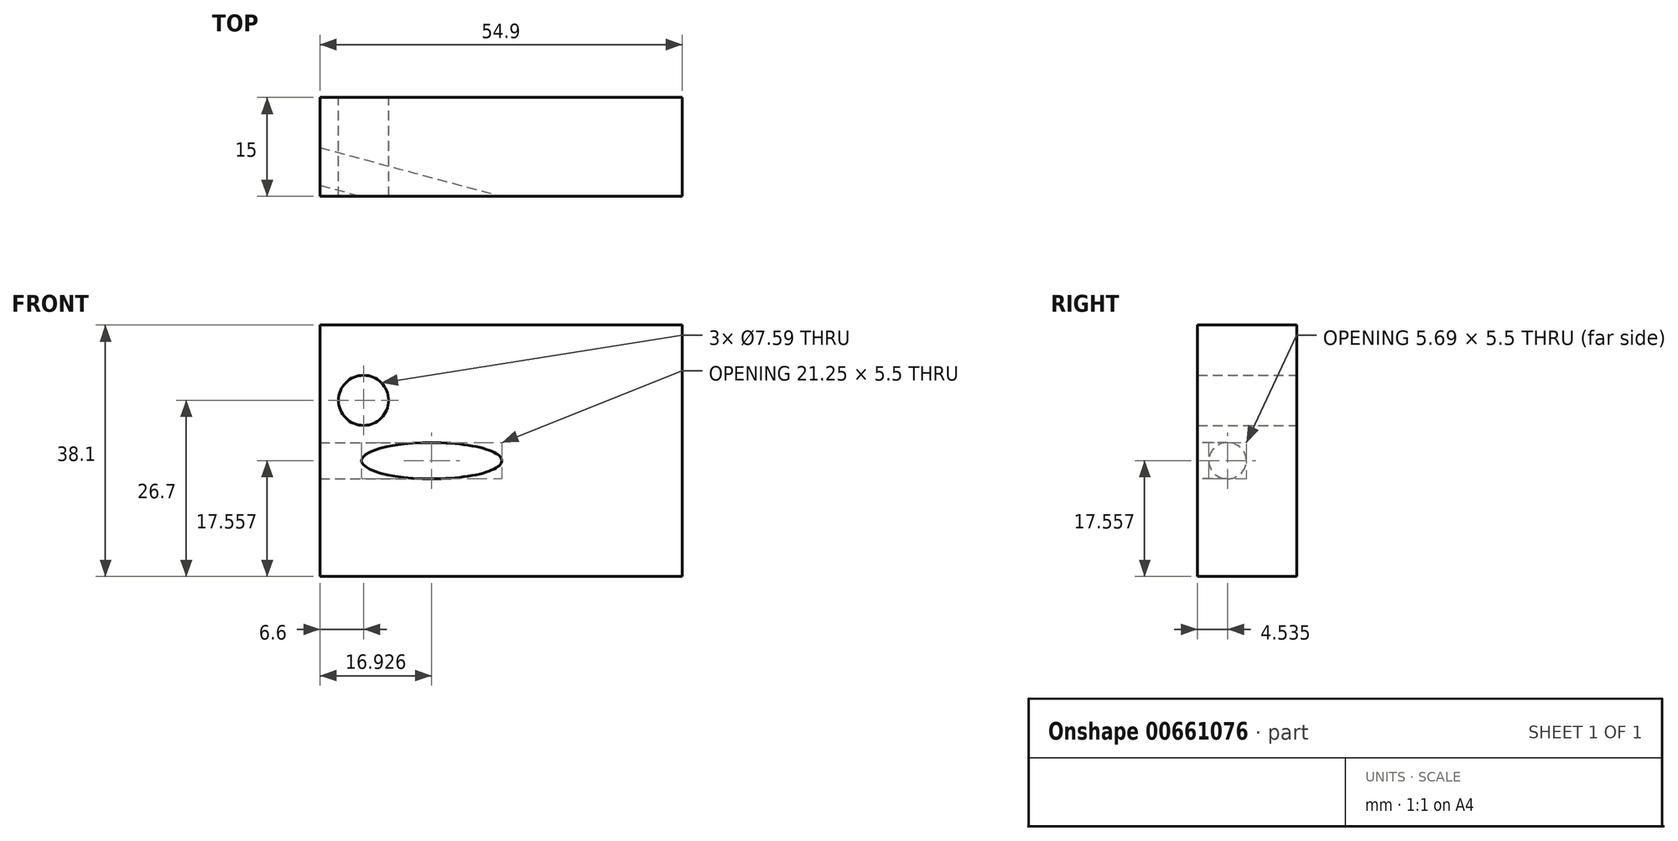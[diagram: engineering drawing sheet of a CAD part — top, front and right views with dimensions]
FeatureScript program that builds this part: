
annotation { "Feature Type Name" : "Feature", "Feature Type Description" : "" }
export const myFeature = defineFeature(function(context is Context, id is Id, definition is map)
    precondition{}
    {
        {
            var Q0;
            Q0=qCreatedBy(makeId("Front.planeOp"),FACE);
            var sketch = newSketch(context, id + "F0", { "sketchPlane" : qUnion([Q0])});
            skLineSegment(sketch, "E0.bottom", {"start": v(-24.75, 17.1) * mm, "end": v(30.15, 17.1) * mm});
            skLineSegment(sketch, "E0.top", {"start": v(-24.75, -21) * mm, "end": v(30.15, -21) * mm});
            skLineSegment(sketch, "E0.left", {"start": v(-24.75, 17.1) * mm, "end": v(-24.75, -21) * mm});
            skLineSegment(sketch, "E0.right", {"start": v(30.15, 17.1) * mm, "end": v(30.15, -21) * mm});
            skSolve(sketch);
        }
        {
            var Q0;
            Q0 = qSketchRegion(id + "F0", true);
            extrude(context, id + "F1", {"entities" : qUnion([Q0]), "depth" : 15 * mm, "offsetDistance" : 25 * mm});
        }
        {
            var Q0;
            Q0=makeQuery(id+"F1.opExtrude","CAP_EDGE",EDGE,{"disambiguationData":[OSD([sQuery(id+"F0.wireOp",EDGE,"E0.right")])],"isStart":false});
            cPlane(context, id + "F2", {"entities" : qUnion([Q0]), "cplaneType" : CPlaneType.LINE_ANGLE, "offset" : 25 * mm, "angle" : 15 * degree, "width" : 150 * mm, "height" : 150 * mm});
        }
        {
            var Q0;
            Q0=qCreatedBy(id+"F2.planeOp",FACE);
            var sketch = newSketch(context, id + "F3", { "sketchPlane" : qUnion([Q0])});
            skPoint(sketch, "E1", {"position": v(16.51, -3.44) * mm});
            skSolve(sketch);
        }
        {
            var Q0;
            Q0=sQuery(id+"F3.wireOp",VERTEX,"E1");
            var Q1;
            Q1=makeQuery(id+"F1.opExtrude","SWEPT_BODY",BODY,{"disambiguationData":[OSD([sQuery(id+"F0.wireOp",EDGE,"E0.bottom"),sQuery(id+"F0.wireOp",EDGE,"E0.top"),sQuery(id+"F0.wireOp",EDGE,"E0.left"),sQuery(id+"F0.wireOp",EDGE,"E0.right")])]});
            hole(context, id + "F4", {"style" : HoleStyle.SIMPLE, "endStyle" : HoleEndStyle.THROUGH, "oppositeDirection" : true, "standardTappedOrClearance" : lookupTablePath({ "standard" : "ISO", "fit" : "Normal", "size" : "M5", "type" : "Clearance" }), "standardBlindInLast" : lookupTablePath({ "fit" : "Standard", "standard" : "ISO", "size" : "M5", "type" : "Clearance" }), "holeDiameter" : 5.5 * mm, "majorDiameter" : 5 * mm, "isTappedThrough" : true, "tappedDepth" : 12 * mm, "tapClearance" : 3, "startFromSketch" : true, "locations" : qUnion([Q0]), "scope" : qUnion([Q1])});
        }
        {
            var Q0;
            Q0=qCreatedBy(makeId("Front.planeOp"),FACE);
            var sketch = newSketch(context, id + "F5", { "sketchPlane" : qUnion([Q0])});
            skCircle(sketch, "E2", {"center": v(-18.15, 5.7) * mm, "radius": 3.8 * mm});
            skSolve(sketch);
        }
        {
            var Q0;
            Q0 = qSketchRegion(id + "F5", true);
            extrude(context, id + "F6", {"entities" : qUnion([Q0]), "operationType" : NewBodyOperationType.REMOVE, "depth" : 25 * mm, "offsetDistance" : 25 * mm});
        }
    });
